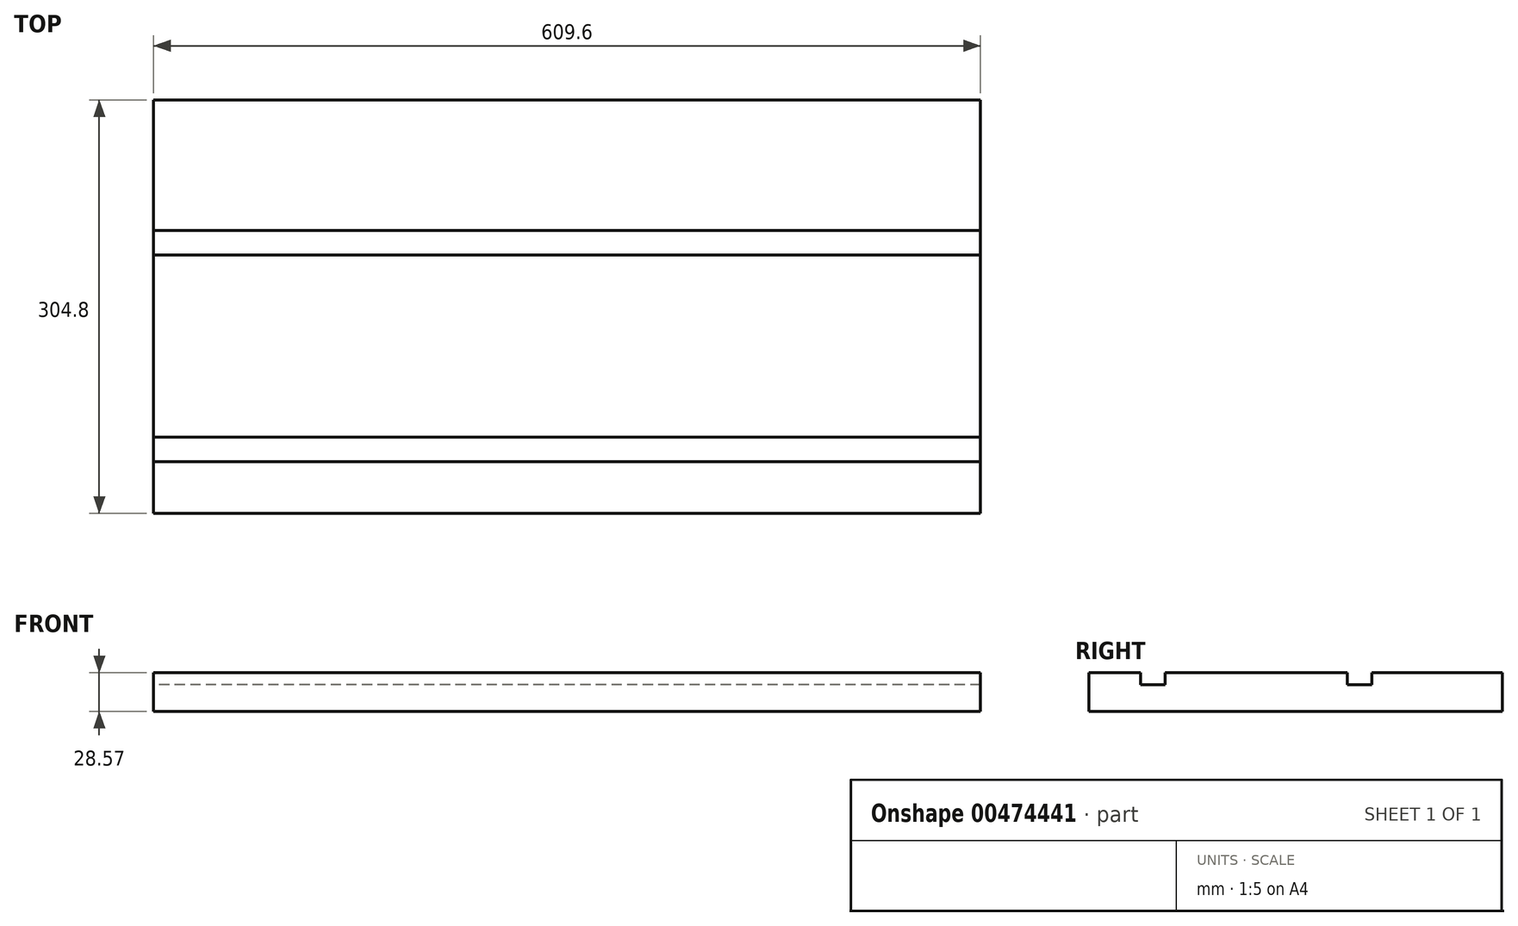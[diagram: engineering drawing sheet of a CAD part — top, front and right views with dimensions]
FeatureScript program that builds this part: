
annotation { "Feature Type Name" : "Feature", "Feature Type Description" : "" }
export const myFeature = defineFeature(function(context is Context, id is Id, definition is map)
    precondition{}
    {
        {
            var Q0;
            Q0=qCreatedBy(makeId("Front.planeOp"),FACE);
            var sketch = newSketch(context, id + "F0", { "sketchPlane" : qUnion([Q0])});
            skLineSegment(sketch, "E0.bottom", {"start": v(0, 0) * mm, "end": v(609.6, 0) * mm});
            skLineSegment(sketch, "E0.top", {"start": v(0, 28.58) * mm, "end": v(609.6, 28.58) * mm});
            skLineSegment(sketch, "E0.left", {"start": v(0, 0) * mm, "end": v(0, 28.58) * mm});
            skLineSegment(sketch, "E0.right", {"start": v(609.6, 0) * mm, "end": v(609.6, 28.58) * mm});
            skSolve(sketch);
        }
        {
            var Q0;
            Q0 = qSketchRegion(id + "F0", true);
            extrude(context, id + "F1", {"entities" : qUnion([Q0]), "oppositeDirection" : true, "depth" : 304.8 * mm, "offsetDistance" : 25.4 * mm});
        }
        {
            var Q0;
            Q0=qCreatedBy(makeId("Right.planeOp"),FACE);
            var sketch = newSketch(context, id + "F2", { "sketchPlane" : qUnion([Q0])});
            skLineSegment(sketch, "E1.bottom", {"start": v(56.12, 28.57) * mm, "end": v(38.1, 28.57) * mm});
            skLineSegment(sketch, "E1.top", {"start": v(56.12, 19.76) * mm, "end": v(38.1, 19.76) * mm});
            skLineSegment(sketch, "E1.left", {"start": v(56.12, 28.57) * mm, "end": v(56.12, 19.76) * mm});
            skLineSegment(sketch, "E1.right", {"start": v(38.1, 28.57) * mm, "end": v(38.1, 19.76) * mm});
            skLineSegment(sketch, "E2.1.0.0", {"start": v(208.52, 28.57) * mm, "end": v(190.5, 28.57) * mm});
            skLineSegment(sketch, "E2.1.0.1", {"start": v(208.52, 28.57) * mm, "end": v(208.52, 19.76) * mm});
            skLineSegment(sketch, "E2.1.0.2", {"start": v(190.5, 28.57) * mm, "end": v(190.5, 19.76) * mm});
            skLineSegment(sketch, "E2.1.0.3", {"start": v(208.52, 19.76) * mm, "end": v(190.5, 19.76) * mm});
            skLineSegment(sketch, "E2.direction1", {"start": v(38.1, 19.76) * mm, "end": v(190.5, 19.76) * mm, "construction": true});
            skSolve(sketch);
        }
        {
            var Q0;
            Q0=makeQuery(id+"F2.imprint","IMPRINT",FACE,{"disambiguationData":[TD([[makeQuery(id+"F2.imprint","IMPRINT",EDGE,{"derivedFrom":sQuery(id+"F2.wireOp",EDGE,"E2.1.0.0")}),1.0]])]});
            var Q1;
            Q1=makeQuery(id+"F2.imprint","IMPRINT",FACE,{"disambiguationData":[TD([[makeQuery(id+"F2.imprint","IMPRINT",EDGE,{"derivedFrom":sQuery(id+"F2.wireOp",EDGE,"E1.bottom")}),1.0]])]});
            extrude(context, id + "F3", {"entities" : qUnion([Q0, Q1]), "operationType" : NewBodyOperationType.REMOVE, "depth" : 609.6 * mm, "offsetDistance" : 25.4 * mm});
        }
    });
